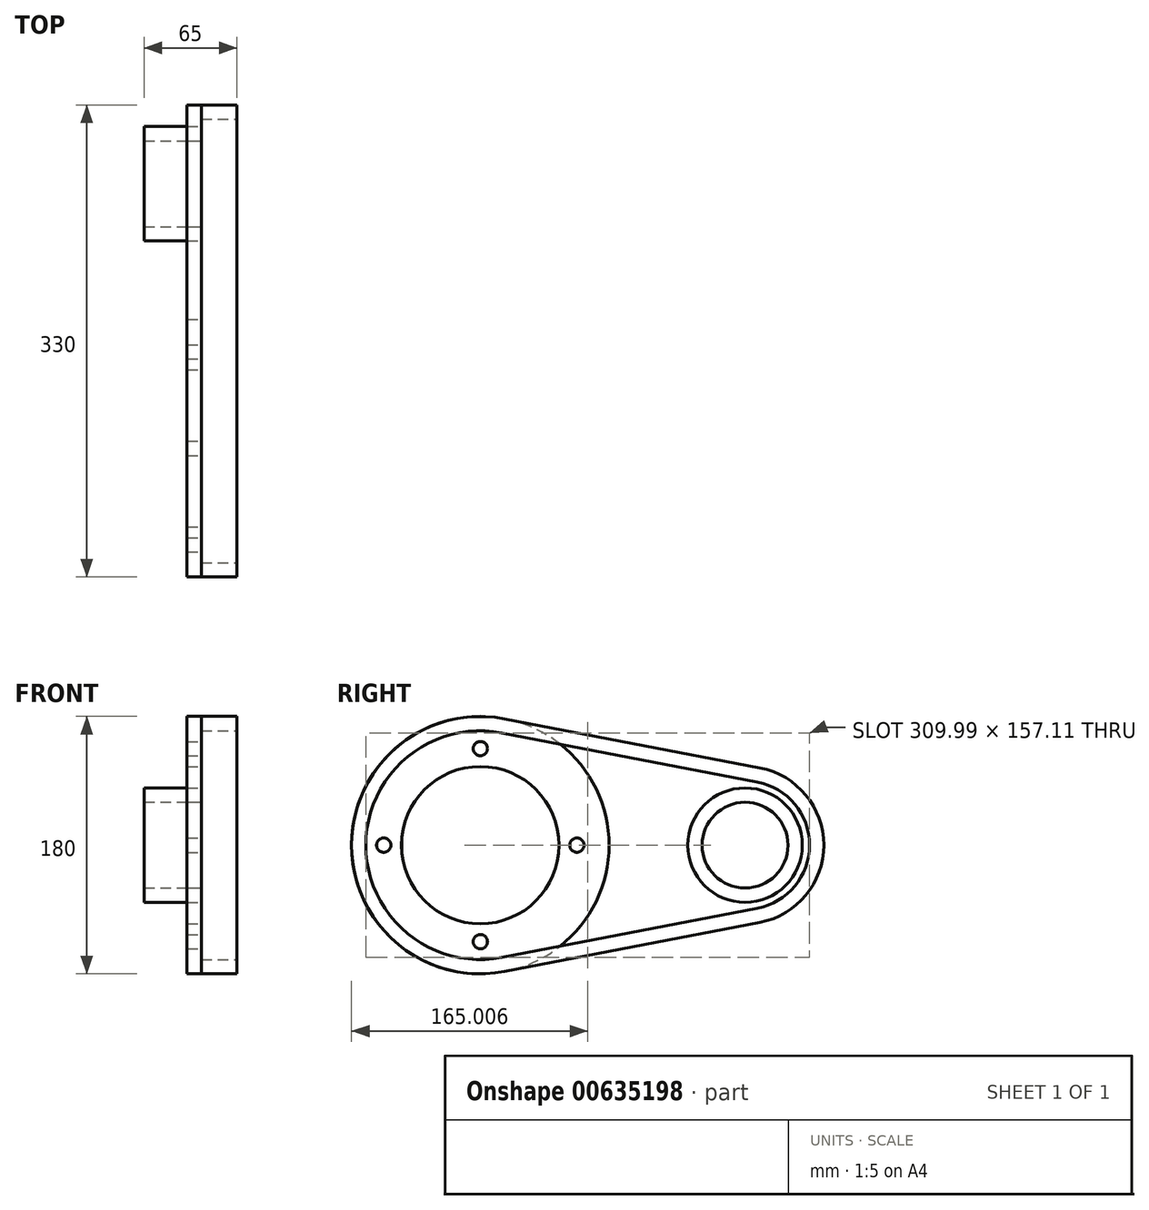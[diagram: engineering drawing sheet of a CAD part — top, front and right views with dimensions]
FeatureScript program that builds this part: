
annotation { "Feature Type Name" : "Feature", "Feature Type Description" : "" }
export const myFeature = defineFeature(function(context is Context, id is Id, definition is map)
    precondition{}
    {
        {
            var Q0;
            Q0=qCreatedBy(makeId("Right.planeOp"),FACE);
            var sketch = newSketch(context, id + "F0", { "sketchPlane" : qUnion([Q0])});
            skCircle(sketch, "E0", {"center": v(0, 0) * mm, "radius": 30 * mm});
            skCircle(sketch, "E1", {"center": v(-185, 0) * mm, "radius": 90 * mm});
            skCircle(sketch, "E2", {"center": v(-185, 0) * mm, "radius": 55 * mm});
            skCircle(sketch, "E3", {"center": v(0, 0) * mm, "radius": 40 * mm});
            skCircle(sketch, "E4", {"center": v(-117.5, 0) * mm, "radius": 5 * mm});
            skCircle(sketch, "E5.1.0", {"center": v(-185, 67.5) * mm, "radius": 5 * mm});
            skCircle(sketch, "E5.2.0", {"center": v(-252.5, 0) * mm, "radius": 5 * mm});
            skCircle(sketch, "E6.1.3.0", {"center": v(-185, -67.5) * mm, "radius": 5 * mm});
            skSolve(sketch);
        }
        {
            var Q0;
            Q0=makeQuery(id+"F0.imprint","IMPRINT",FACE,{"disambiguationData":[TD([[makeQuery(id+"F0.imprint","IMPRINT",EDGE,{"derivedFrom":sQuery(id+"F0.wireOp",EDGE,"E0")}),-1.0]])]});
            extrude(context, id + "F1", {"entities" : qUnion([Q0]), "depth" : -70 * mm, "offsetDistance" : 25 * mm, "hasSecondDirection" : true, "secondDirectionOppositeDirection" : true, "secondDirectionDepth" : 30 * mm});
        }
        {
            var Q0;
            Q0=makeQuery(id+"F0.imprint","IMPRINT",FACE,{"disambiguationData":[TD([[makeQuery(id+"F0.imprint","IMPRINT",EDGE,{"derivedFrom":sQuery(id+"F0.wireOp",EDGE,"E1")}),1.0]])]});
            extrude(context, id + "F2", {"entities" : qUnion([Q0]), "depth" : -40 * mm, "offsetDistance" : 25 * mm, "hasSecondDirection" : true, "secondDirectionOppositeDirection" : true, "secondDirectionDepth" : 30 * mm});
        }
        {
            var Q0;
            Q0=qCreatedBy(makeId("Right.planeOp"),FACE);
            var sketch = newSketch(context, id + "F3", { "sketchPlane" : qUnion([Q0])});
            skArc(sketch, "E7", {"start": v(10.4, -54) * mm, "mid": v(55, 0) * mm, "end": v(10.4, 54) * mm});
            skCircle(sketch, "E8", {"center": v(0, 0) * mm, "radius": 30 * mm});
            skArc(sketch, "E9", {"start": v(-167.96, 88.37) * mm, "mid": v(-274.99, 0) * mm, "end": v(-167.96, -88.37) * mm});
            skLineSegment(sketch, "E10", {"start": v(-167.96, 88.37) * mm, "end": v(10.4, 54) * mm});
            skLineSegment(sketch, "E11.MirrorCS", {"start": v(-167.96, -88.37) * mm, "end": v(10.4, -54) * mm});
            skArc(sketch, "E12.MirrorC", {"start": v(-167.96, -88.37) * mm, "mid": v(-274.99, 0) * mm, "end": v(-167.96, 88.37) * mm});
            skArc(sketch, "E13.MirrorC", {"start": v(10.4, 54) * mm, "mid": v(55, 0) * mm, "end": v(10.4, -54) * mm});
            skCircle(sketch, "E14", {"center": v(-184.99, 0) * mm, "radius": 55 * mm});
            skCircle(sketch, "E15", {"center": v(-117.5, 0) * mm, "radius": 5 * mm});
            skCircle(sketch, "E16.1.0", {"center": v(-184.99, 67.49) * mm, "radius": 5 * mm});
            skCircle(sketch, "E16.2.0", {"center": v(-252.48, 0) * mm, "radius": 5 * mm});
            skCircle(sketch, "E16.3.0", {"center": v(-184.99, -67.49) * mm, "radius": 5 * mm});
            skSolve(sketch);
        }
        {
            var Q0;
            Q0=makeQuery(id+"F3.imprint","IMPRINT",FACE,{"disambiguationData":[TD([[makeQuery(id+"F3.imprint","IMPRINT",EDGE,{"derivedFrom":sQuery(id+"F3.wireOp",EDGE,"E8")}),-1.0]])]});
            extrude(context, id + "F4", {"entities" : qUnion([Q0]), "depth" : -40 * mm, "offsetDistance" : 25 * mm, "hasSecondDirection" : true, "secondDirectionOppositeDirection" : true, "secondDirectionDepth" : 30 * mm});
        }
        {
            var Q0;
            Q0=qCreatedBy(makeId("Right.planeOp"),FACE);
            var sketch = newSketch(context, id + "F5", { "sketchPlane" : qUnion([Q0])});
            skArc(sketch, "E17.0", {"start": v(-169.85, -78.56) * mm, "mid": v(-264.99, 0) * mm, "end": v(-169.85, 78.56) * mm});
            skLineSegment(sketch, "E17.1", {"start": v(-169.85, -78.56) * mm, "end": v(8.51, -44.19) * mm});
            skArc(sketch, "E17.2", {"start": v(8.51, 44.19) * mm, "mid": v(45, 0) * mm, "end": v(8.51, -44.19) * mm});
            skLineSegment(sketch, "E17.3", {"start": v(-169.85, 78.56) * mm, "end": v(8.51, 44.19) * mm});
            skArc(sketch, "E18.0", {"start": v(-167.96, -88.37) * mm, "mid": v(-274.99, 0) * mm, "end": v(-167.96, 88.37) * mm});
            skLineSegment(sketch, "E18.1", {"start": v(-167.96, -88.37) * mm, "end": v(10.4, -54) * mm});
            skArc(sketch, "E18.2", {"start": v(10.4, 54) * mm, "mid": v(55, 0) * mm, "end": v(10.4, -54) * mm});
            skLineSegment(sketch, "E18.3", {"start": v(-167.96, 88.37) * mm, "end": v(10.4, 54) * mm});
            skSolve(sketch);
        }
        {
            var Q0;
            Q0 = qSketchRegion(id + "F5", true);
            extrude(context, id + "F6", {"entities" : qUnion([Q0]), "depth" : -30 * mm, "offsetDistance" : 25 * mm, "hasSecondDirection" : true, "secondDirectionOppositeDirection" : true, "secondDirectionDepth" : 5 * mm});
        }
    });
